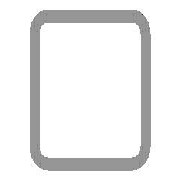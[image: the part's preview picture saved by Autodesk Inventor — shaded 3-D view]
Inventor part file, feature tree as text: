
AUTODESK INVENTOR PART (.ipt)
format: ipt  version: 2016 (Build 200138000, 138)  size: 134,656 bytes
history: native  units: mm (DEFAULTED — no unit token found)
features: other x4, plane x3, sketch x3, split x2
ambient origin geometry x8: Origin, YZ Plane, XZ Plane, XY Plane, X Axis, Y Axis, Z Axis, Center Point
bodies: Solid1 (feature_tree), Body (feature_tree)
feature tree (12):
  parser-record x1  (decoder bookkeeping rows leaked as tree rows — omitted from the tree; the rows remain in map.json)
  other  "Driven Length"
  other  "Start plane"
  other  "End plane"
  plane  "Work Plane4"
  split  "Split1"
  plane  "Work Plane5"
  split  "Split2"
  sketch  "Sketch"  dims[d7=4.0mm d9=25.0mm d11=25.0mm d12=2.0mm d13=25.0mm d14=455.0mm d15=12.5mm d16=12.5mm d17=90.0deg d18=430.0mm]
  sketch  "Sketch3"  dims[d3=430.0mm]
  plane  "Work Plane3"
  sketch  "Sketch4"  dims[d4=0.0mm]
